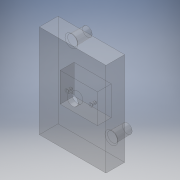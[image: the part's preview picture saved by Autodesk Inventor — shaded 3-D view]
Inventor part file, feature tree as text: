
AUTODESK INVENTOR PART (.ipt)
format: ipt  version: 2019 (Build 230136000, 136)  size: 160,768 bytes
history: native  units: mm
features: reference x14, other x5, extrude x4, sketch x4, fillet x3
ambient origin geometry x8: Origin, YZ Plane, XZ Plane, XY Plane, X Axis, Y Axis, Z Axis, Center Point
bodies: Solid1 (feature_tree)
feature tree (30):
  extrude  "Extrusion1"  Depth=7.0mm TaperAngle=0.0deg
  extrude  "Extrusion3"  Depth=6.0mm
  extrude  "Extrusion4"  Depth=5.2mm
  extrude  "Extrusion5"  Depth=0.2mm
  fillet  "Fillet1"  Radius=0.4mm
  fillet  "Fillet2"  Radius=0.5mm
  fillet  "Fillet3"  Radius=1.0mm
  sketch  "Sketch1"  dims[d0=4.1mm d1=7.0mm d2=0.0mm]
  reference  "Reference1"
  reference  "Reference2"
  reference  "Reference3"
  reference  "Reference4"
  sketch  "Sketch2"  dims[d9=3.8mm d10=6.0mm d11=-0.174533mm]
  reference  "Reference5"
  reference  "Reference6"
  sketch  "Sketch3"  dims[d16=5.2mm d17=0.0mm d18=1.0mm]
  reference  "Reference12"
  reference  "Reference14"
  sketch  "Sketch4"  dims[d19=2.0mm d20=0.0mm d21=0.2mm d22=0.4mm d23=0.5mm d28=1.0mm d29=1.0mm d30=0.2mm d31=0.2mm]
  reference  "Reference15"
  reference  "Reference16"
  reference  "Reference17"
  reference  "Reference18"
  reference  "Reference19"
  reference  "Reference20"
  parser-record x1  (decoder bookkeeping rows leaked as tree rows — omitted from the tree; the rows remain in map.json)
  other  "Kinematics.iam"
  other  "Base:1"
  other  "Motor-GM15BY:1"
  other  "Motor-Body:1"
note: 1 file-system path scrubbed to <path> (originals preserved in map.json)
